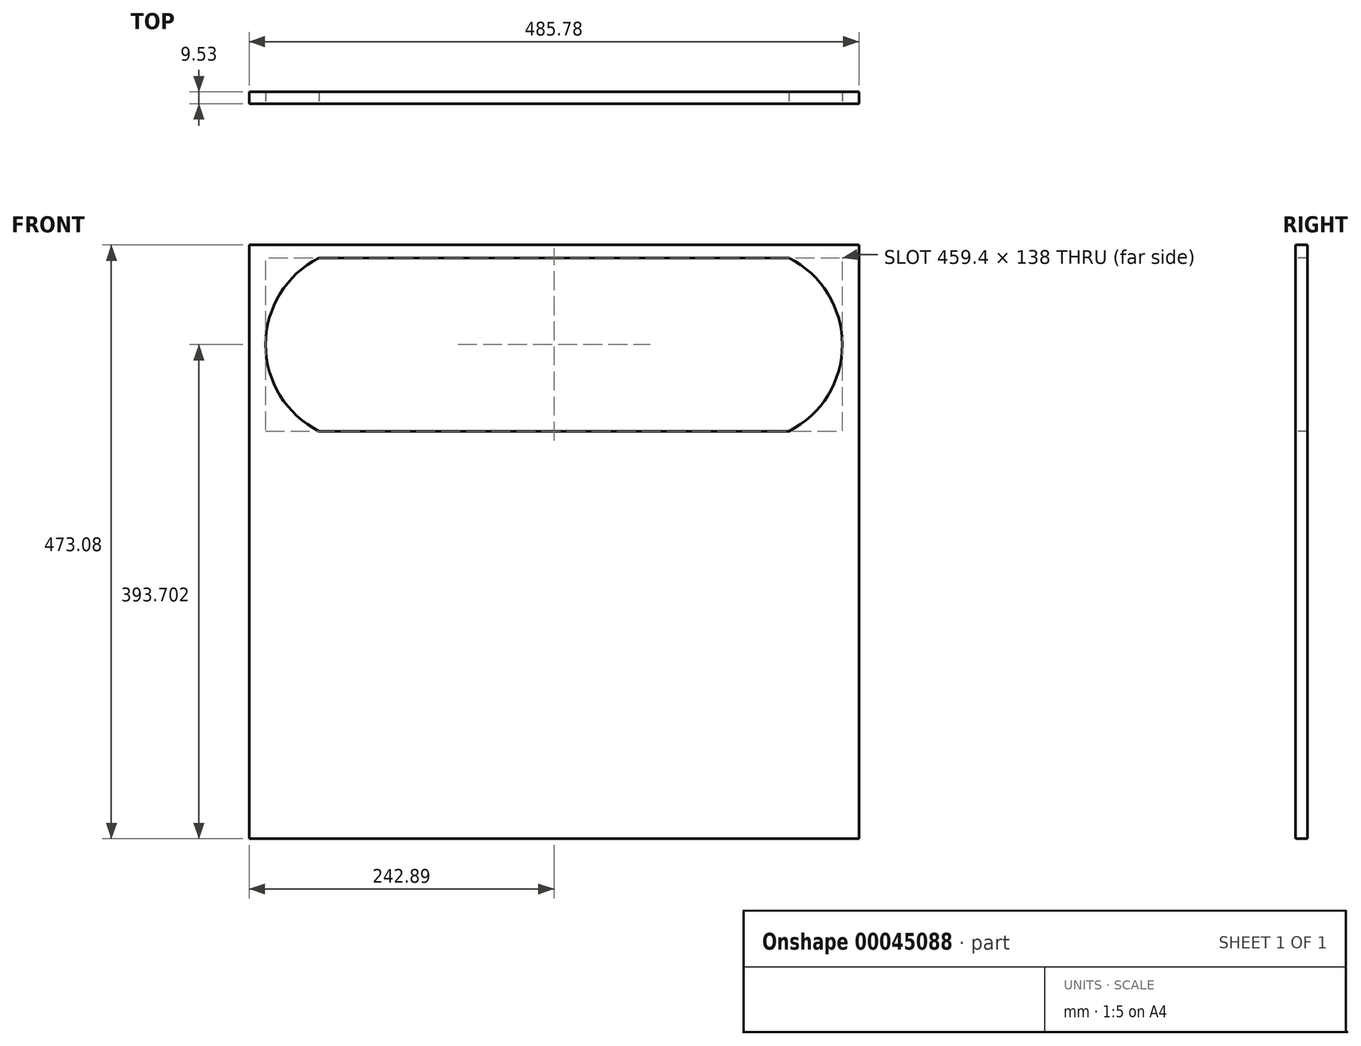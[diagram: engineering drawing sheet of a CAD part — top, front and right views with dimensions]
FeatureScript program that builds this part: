
annotation { "Feature Type Name" : "Feature", "Feature Type Description" : "" }
export const myFeature = defineFeature(function(context is Context, id is Id, definition is map)
    precondition{}
    {
        {
            var Q0;
            Q0=qCreatedBy(makeId("Front.planeOp"),FACE);
            var sketch = newSketch(context, id + "F0", { "sketchPlane" : qUnion([Q0])});
            skLineSegment(sketch, "E0.rect.bottom", {"start": v(-242.89, 236.54) * mm, "end": v(242.89, 236.54) * mm});
            skLineSegment(sketch, "E0.rect.top", {"start": v(-242.89, -236.54) * mm, "end": v(242.89, -236.54) * mm});
            skLineSegment(sketch, "E0.rect.left", {"start": v(-242.89, 236.54) * mm, "end": v(-242.89, -236.54) * mm});
            skLineSegment(sketch, "E0.rect.right", {"start": v(242.89, 236.54) * mm, "end": v(242.89, -236.54) * mm});
            skPoint(sketch, "E0.rect.middle", {"position": v(0, 0) * mm});
            skSolve(sketch);
        }
        {
            var Q0;
            Q0 = qSketchRegion(id + "F0", true);
            extrude(context, id + "F1", {"entities" : qUnion([Q0]), "depth" : 9.52 * mm});
        }
        {
            var Q0;
            Q0=makeQuery(id+"F1.opExtrude","CAP_FACE",FACE,{"disambiguationData":[OSD([sQuery(id+"F0.wireOp",EDGE,"E0.rect.bottom"),sQuery(id+"F0.wireOp",EDGE,"E0.rect.top"),sQuery(id+"F0.wireOp",EDGE,"E0.rect.left"),sQuery(id+"F0.wireOp",EDGE,"E0.rect.right")])],"isStart":false});
            var sketch = newSketch(context, id + "F2", { "sketchPlane" : qUnion([Q0])});
            skLineSegment(sketch, "E1", {"start": v(0, 236.54) * mm, "end": v(0, -236.54) * mm, "construction": true});
            skLineSegment(sketch, "E2", {"start": v(-242.89, 157.16) * mm, "end": v(242.89, 157.16) * mm, "construction": true});
            skPoint(sketch, "E3", {"position": v(0, 157.16) * mm});
            skPoint(sketch, "E4", {"position": v(-152.44, 157.16) * mm});
            skPoint(sketch, "E5.MirrorP", {"position": v(152.44, 157.16) * mm});
            skArc(sketch, "E6", {"start": v(-187.19, 226.16) * mm, "mid": v(-229.7, 157.16) * mm, "end": v(-187.19, 88.16) * mm});
            skArc(sketch, "E7.MirrorC", {"start": v(187.19, 226.16) * mm, "mid": v(229.7, 157.16) * mm, "end": v(187.19, 88.16) * mm});
            skLineSegment(sketch, "E8", {"start": v(-152.44, 157.16) * mm, "end": v(-152.44, 234.42) * mm, "construction": true});
            skLineSegment(sketch, "E9", {"start": v(152.44, 157.16) * mm, "end": v(152.44, 79.9) * mm, "construction": true});
            skLineSegment(sketch, "E10", {"start": v(-152.44, 157.16) * mm, "end": v(-152.44, 88.16) * mm, "construction": true});
            skLineSegment(sketch, "E11", {"start": v(152.44, 157.16) * mm, "end": v(152.44, 226.16) * mm, "construction": true});
            skLineSegment(sketch, "E12.bottom", {"start": v(152.44, 226.16) * mm, "end": v(-152.44, 226.16) * mm});
            skLineSegment(sketch, "E12.top", {"start": v(152.44, 88.16) * mm, "end": v(-152.44, 88.16) * mm});
            skLineSegment(sketch, "E13", {"start": v(-152.44, 226.16) * mm, "end": v(-187.19, 226.16) * mm});
            skLineSegment(sketch, "E14", {"start": v(152.44, 226.16) * mm, "end": v(187.19, 226.16) * mm});
            skLineSegment(sketch, "E15", {"start": v(152.44, 88.16) * mm, "end": v(187.19, 88.16) * mm});
            skLineSegment(sketch, "E16", {"start": v(-152.44, 88.16) * mm, "end": v(-187.19, 88.16) * mm});
            skSolve(sketch);
        }
        {
            var Q0;
            Q0=sQuery(id+"F2.wireOp",VERTEX,"E3");
            var Q1;
            Q1=makeQuery(id+"F1.opExtrude","SWEPT_BODY",BODY,{"disambiguationData":[OSD([sQuery(id+"F0.wireOp",EDGE,"E0.rect.bottom"),sQuery(id+"F0.wireOp",EDGE,"E0.rect.top"),sQuery(id+"F0.wireOp",EDGE,"E0.rect.left"),sQuery(id+"F0.wireOp",EDGE,"E0.rect.right")])]});
            hole(context, id + "F3", {"style" : HoleStyle.SIMPLE, "holeDiameter" : 109.98 * mm, "endStyle" : HoleEndStyle.THROUGH, "locations" : qUnion([Q0]), "scope" : qUnion([Q1])});
        }
        {
            var Q0;
            Q0 = qSketchRegion(id + "F2", true);
            extrude(context, id + "F4", {"entities" : qUnion([Q0]), "operationType" : NewBodyOperationType.REMOVE, "oppositeDirection" : true, "depth" : 25.4 * mm});
        }
    });
